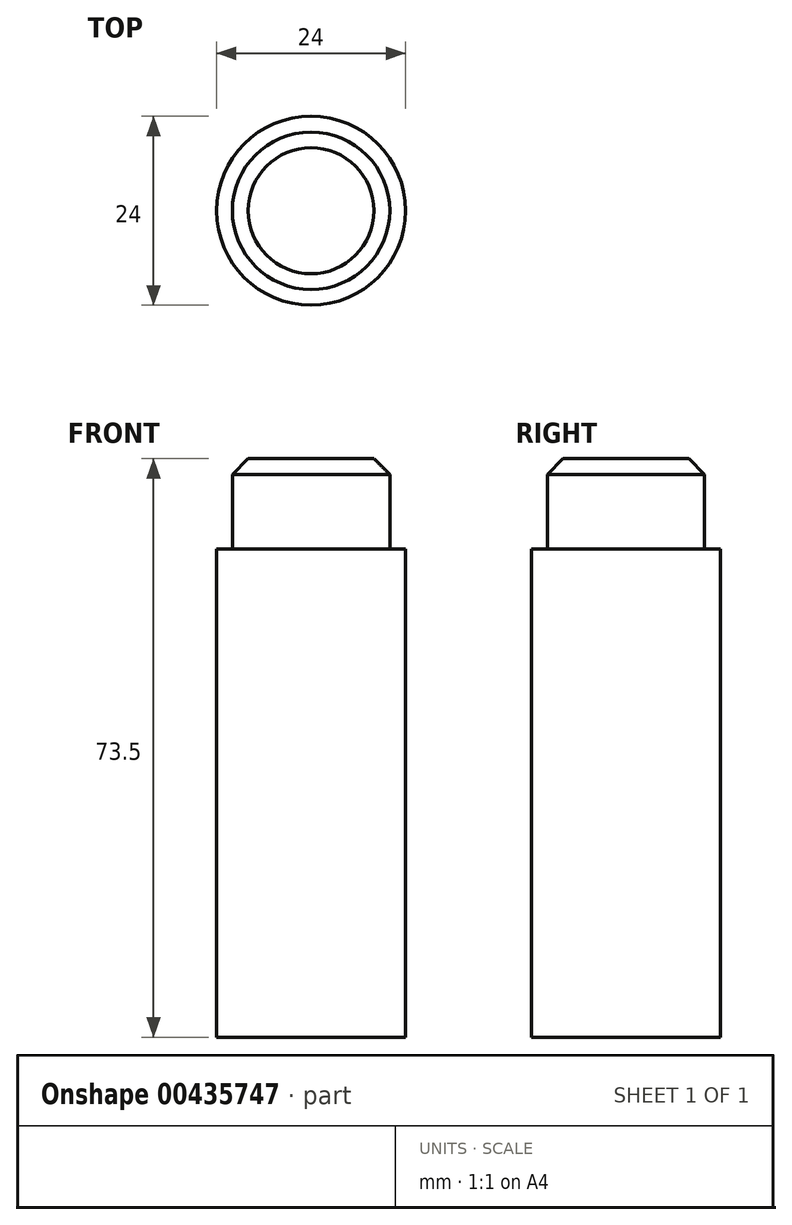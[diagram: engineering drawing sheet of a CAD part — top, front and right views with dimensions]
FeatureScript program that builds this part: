
annotation { "Feature Type Name" : "Feature", "Feature Type Description" : "" }
export const myFeature = defineFeature(function(context is Context, id is Id, definition is map)
    precondition{}
    {
        {
            var Q0;
            Q0=qCreatedBy(makeId("Top.planeOp"),FACE);
            var sketch = newSketch(context, id + "F0", { "sketchPlane" : qUnion([Q0])});
            skCircle(sketch, "E0", {"center": v(0, 0) * mm, "radius": 12 * mm});
            skSolve(sketch);
        }
        {
            var Q0;
            Q0=makeQuery(id+"F0.imprint","IMPRINT",FACE,{"disambiguationData":[TD([[makeQuery(id+"F0.imprint","IMPRINT",EDGE,{"derivedFrom":sQuery(id+"F0.wireOp",EDGE,"E0")}),1.0]])]});
            extrude(context, id + "F1", {"entities" : qUnion([Q0]), "endBound" : BoundingType.SYMMETRIC, "depth" : 62 * mm});
        }
        {
            var Q0;
            Q0=makeQuery(id+"F1.opExtrude","CAP_FACE",FACE,{"disambiguationData":[OSD([sQuery(id+"F0.wireOp",EDGE,"E0")])],"isStart":false});
            var sketch = newSketch(context, id + "F2", { "sketchPlane" : qUnion([Q0])});
            skCircle(sketch, "E1", {"center": v(0, 0) * mm, "radius": 10 * mm});
            skSolve(sketch);
        }
        {
            var Q0;
            Q0=makeQuery(id+"F2.imprint","IMPRINT",FACE,{"disambiguationData":[TD([[makeQuery(id+"F2.imprint","IMPRINT",EDGE,{"derivedFrom":sQuery(id+"F2.wireOp",EDGE,"E1")}),1.0]])]});
            extrude(context, id + "F3", {"entities" : qUnion([Q0]), "operationType" : NewBodyOperationType.ADD, "depth" : ((78 - 55) / 2) * mm});
        }
        {
            var Q0;
            Q0=makeQuery(id+"F3.opExtrude","CAP_EDGE",EDGE,{"disambiguationData":[OSD([sQuery(id+"F2.wireOp",EDGE,"E1")])],"isStart":false});
            var Q1;
            Q1=makeQuery(id+"FgBE6GKZ8LE3eSN_1.1.F3.opExtrude","CAP_EDGE",EDGE,{"disambiguationData":[OSD([sQuery(id+"F2.wireOp",EDGE,"E1")])],"isStart":false});
            chamfer(context, id + "F4", {"entities" : qUnion([Q0, Q1]), "width" : 2 * mm, "tangentPropagation" : true});
        }
    });
